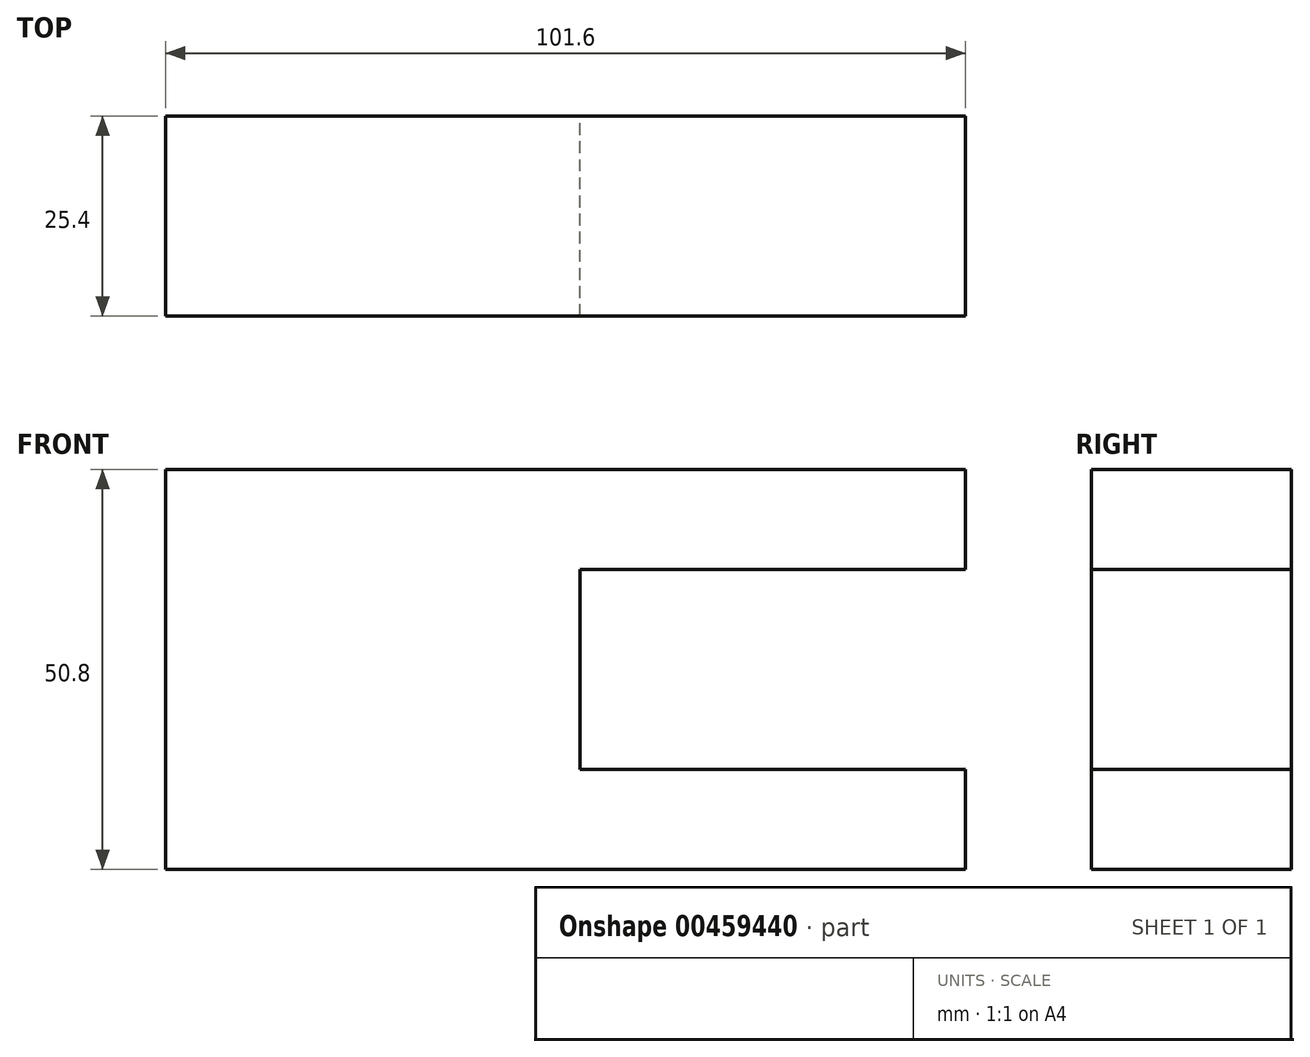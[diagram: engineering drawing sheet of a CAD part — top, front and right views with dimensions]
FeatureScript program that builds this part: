
annotation { "Feature Type Name" : "Feature", "Feature Type Description" : "" }
export const myFeature = defineFeature(function(context is Context, id is Id, definition is map)
    precondition{}
    {
        {
            var Q0;
            Q0=qCreatedBy(makeId("Front.planeOp"),FACE);
            var sketch = newSketch(context, id + "F0", { "sketchPlane" : qUnion([Q0])});
            skLineSegment(sketch, "E0.bottom", {"start": v(-50.8, 25.4) * mm, "end": v(50.8, 25.4) * mm});
            skLineSegment(sketch, "E0.top", {"start": v(-50.8, -25.4) * mm, "end": v(50.8, -25.4) * mm});
            skLineSegment(sketch, "E0.left", {"start": v(-50.8, 25.4) * mm, "end": v(-50.8, -25.4) * mm});
            skLineSegment(sketch, "E0.right", {"start": v(50.8, 25.4) * mm, "end": v(50.8, -25.4) * mm});
            skPoint(sketch, "E0.middle", {"position": v(0, 0) * mm});
            skSolve(sketch);
        }
        {
            var Q0;
            Q0=makeQuery(id+"F0.imprint","IMPRINT",FACE,{"disambiguationData":[TD([[makeQuery(id+"F0.imprint","IMPRINT",EDGE,{"derivedFrom":sQuery(id+"F0.wireOp",EDGE,"E0.bottom")}),-1.0]])]});
            extrude(context, id + "F1", {"entities" : qUnion([Q0]), "depth" : 25.4 * mm});
        }
        {
            var Q0;
            Q0=qCreatedBy(makeId("Front.planeOp"),FACE);
            var sketch = newSketch(context, id + "F2", { "sketchPlane" : qUnion([Q0])});
            skLineSegment(sketch, "E1.bottom", {"start": v(52.62, 12.7) * mm, "end": v(1.82, 12.7) * mm});
            skLineSegment(sketch, "E1.top", {"start": v(52.62, -12.7) * mm, "end": v(1.82, -12.7) * mm});
            skLineSegment(sketch, "E1.left", {"start": v(52.62, 12.7) * mm, "end": v(52.62, -12.7) * mm});
            skLineSegment(sketch, "E1.right", {"start": v(1.82, 12.7) * mm, "end": v(1.82, -12.7) * mm});
            skSolve(sketch);
        }
        {
            var Q0;
            Q0 = qSketchRegion(id + "F2", true);
            extrude(context, id + "F3", {"entities" : qUnion([Q0]), "operationType" : NewBodyOperationType.REMOVE, "depth" : 25.4 * mm});
        }
    });
